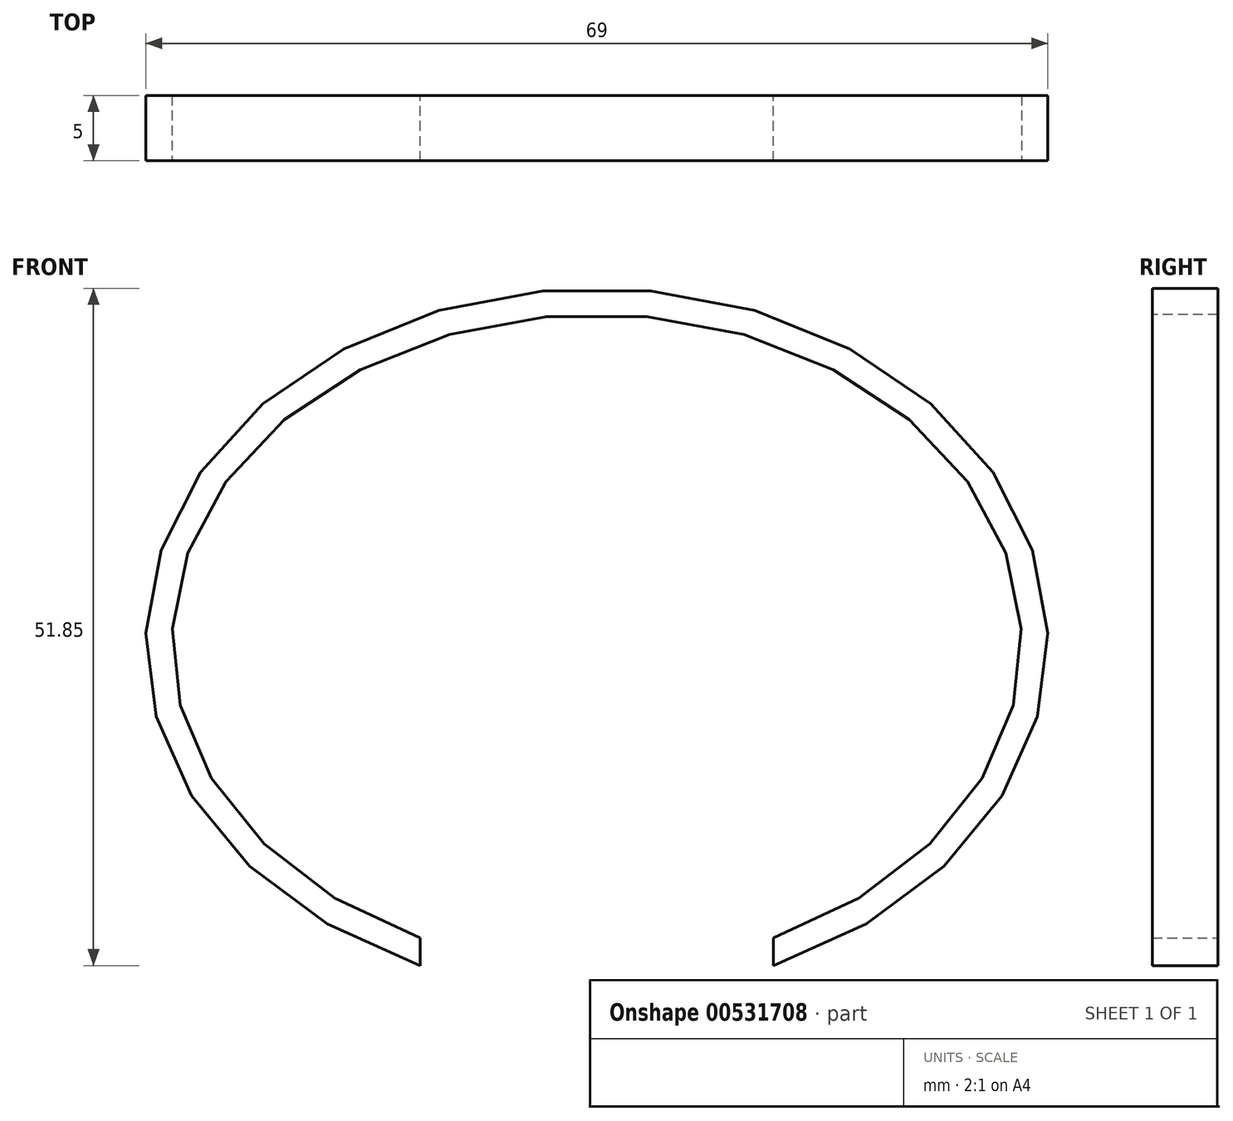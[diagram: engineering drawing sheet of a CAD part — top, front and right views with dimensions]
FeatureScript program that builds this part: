
annotation { "Feature Type Name" : "Feature", "Feature Type Description" : "" }
export const myFeature = defineFeature(function(context is Context, id is Id, definition is map)
    precondition{}
    {
        {
            var Q0;
            Q0=qCreatedBy(makeId("Front.planeOp"),FACE);
            var sketch = newSketch(context, id + "F0", { "sketchPlane" : qUnion([Q0])});
            skEllipticalArc(sketch, "E0", {});
            skEllipticalArc(sketch, "E1", {});
            skPoint(sketch, "E2.oppositeSnap0", {"position": v(0, -27) * mm});
            skLineSegment(sketch, "E2.right", {"start": v(-13.5, -22.74) * mm, "end": v(-13.5, -24.85) * mm});
            skLineSegment(sketch, "E3.MirrorCS", {"start": v(13.5, -22.74) * mm, "end": v(13.5, -24.85) * mm});
            skPoint(sketch, "E4.orphan", {"position": v(0, -20.43) * mm});
            skPoint(sketch, "E5.orphan", {"position": v(-13.5, -27) * mm});
            skPoint(sketch, "E6.orphan", {"position": v(-13.5, -20.43) * mm});
            const initialGuessF0  = {"E0": [0, 0, 1, 0, 0.0325, 0.025, 5.140754561367386, 4.284023399401993], "E1": [0, 0, 1, 0, 0.0345, 0.027, 5.1144375134826925, 4.310340447286686]};
            skSetInitialGuess(sketch, initialGuessF0);
            skSolve(sketch);
        }
        {
            var Q0;
            Q0=makeQuery(id+"F0.imprint","IMPRINT",FACE,{"disambiguationData":[TD([[makeQuery(id+"F0.imprint","IMPRINT",EDGE,{"derivedFrom":sQuery(id+"F0.wireOp",EDGE,"E0")}),-1.0]])]});
            extrude(context, id + "F1", {"entities" : qUnion([Q0]), "depth" : 5 * mm, "offsetDistance" : 25.4 * mm});
        }
    });
